# Revit family: Class-I-Fan_VBBB-CW-THD_Carnes
name_source: partatom
category: Mechanical Equipment
revit_build: Autodesk Revit Architecture 2012 (Build: 20110309_2315(x64)
units: mm (PartAtom-declared; Revit-internal decimal feet)

## types (1)
- See Type Catalog
    01 = 14.88 "
    04 CSI = 23 34 23
    95 CSI = 15830
    A = 13 "
    Angle = 90.00°
    Assembly Code = D3040200
    B = 9.75 "
    C = 13.26 "
    Catalog URL = http://www.carnes.com
    D = 14.5 "
    DX = 1 "
    Default Elevation = 0 "
    Description = Cetrifugal Blowers
    Drip = 4.88 "
    Drip1 = 4.88 "
    G = 16 "
    H = 24.5 "
    HA = 9.75 "
    HC = 13.94 "
    HE = 10.56 "
    HG = 9.31 "
    HJ = 9.25 "
    HN = 12.94 "
    Housing = Aluminum-Carnes-Spun-Brushed
    Housing Rotation CW DBD = Yes
    IOM Instructions URL = http://www.carnes.com
    J = 7.44 "
    KL = 2 "
    Manufacturer = Carnes Company
    Manufacturer Fax = 608-845-6470
    Model = VBBB 12
    Motor Cover = No
    Motor Pedastal Stand = 11.88 "
    P = 19.75 "
    Product Page URL = http://www.carnes.com
    Radius = 6.63 "
    SD = 1 "
    SD Radius = 0.5 "
    SE = 2.75 "
    Support Plate Drip = 17.63 "
    URL = http://www.carnes.com
    Warranty URL = http://www.carnes.com
    Weather Cover = Yes
    Weather Cover Height = 22.38 "
    Weather Cover Length = 17.38 "
    Weather Cover Width = 16 "
    ecoScorecard Product Page = http://ecoscorecard.com

## geometry (parser evidence)
native form markers: Sweep x40
no freeform markers — native parametric forms only
